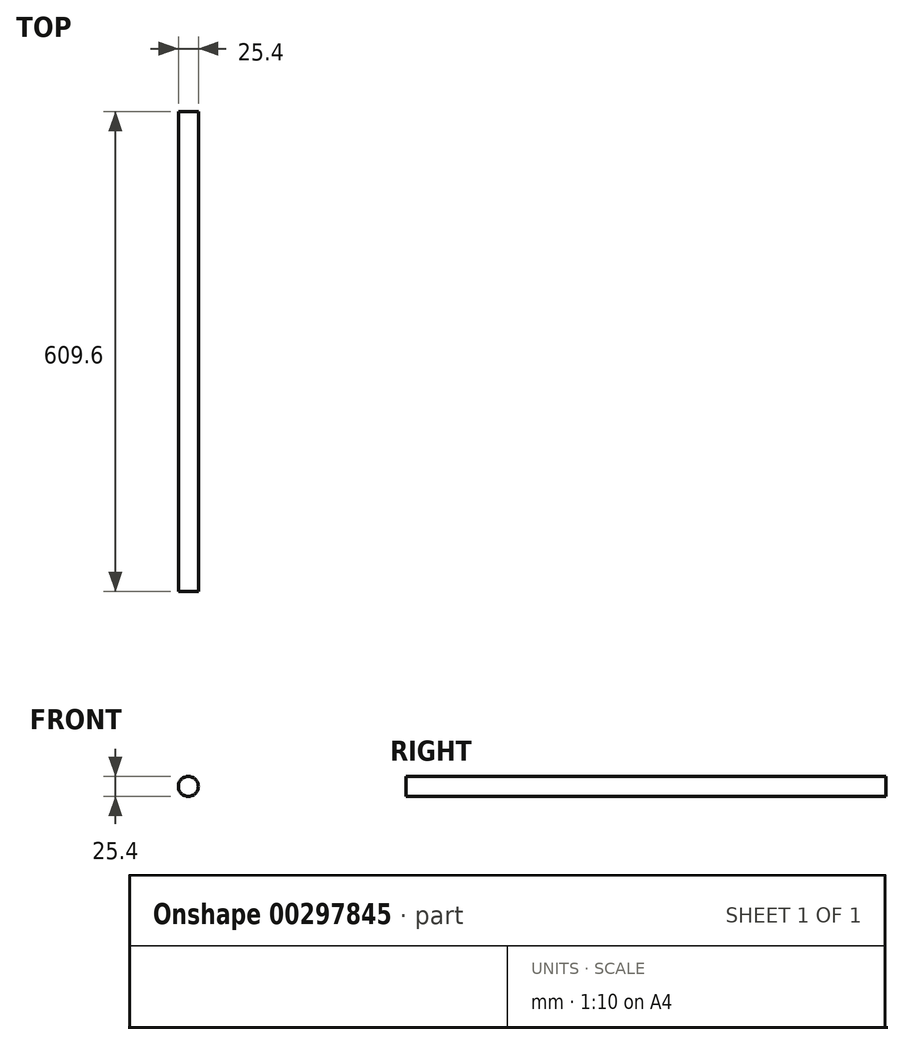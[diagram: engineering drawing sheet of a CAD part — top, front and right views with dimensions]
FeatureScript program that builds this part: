
annotation { "Feature Type Name" : "Feature", "Feature Type Description" : "" }
export const myFeature = defineFeature(function(context is Context, id is Id, definition is map)
    precondition{}
    {
        {
            var Q0;
            Q0=qCreatedBy(makeId("Front.planeOp"),FACE);
            var sketch = newSketch(context, id + "F0", { "sketchPlane" : qUnion([Q0])});
            skCircle(sketch, "E0", {"center": v(0, 0) * mm, "radius": 12.7 * mm});
            skSolve(sketch);
        }
        {
            var Q0;
            Q0=makeQuery(id+"F0.imprint","IMPRINT",FACE,{"disambiguationData":[TD([[makeQuery(id+"F0.imprint","IMPRINT",EDGE,{"derivedFrom":sQuery(id+"F0.wireOp",EDGE,"E0")}),1.0]])]});
            extrude(context, id + "F1", {"entities" : qUnion([Q0]), "oppositeDirection" : true, "depth" : 609.6 * mm});
        }
    });
